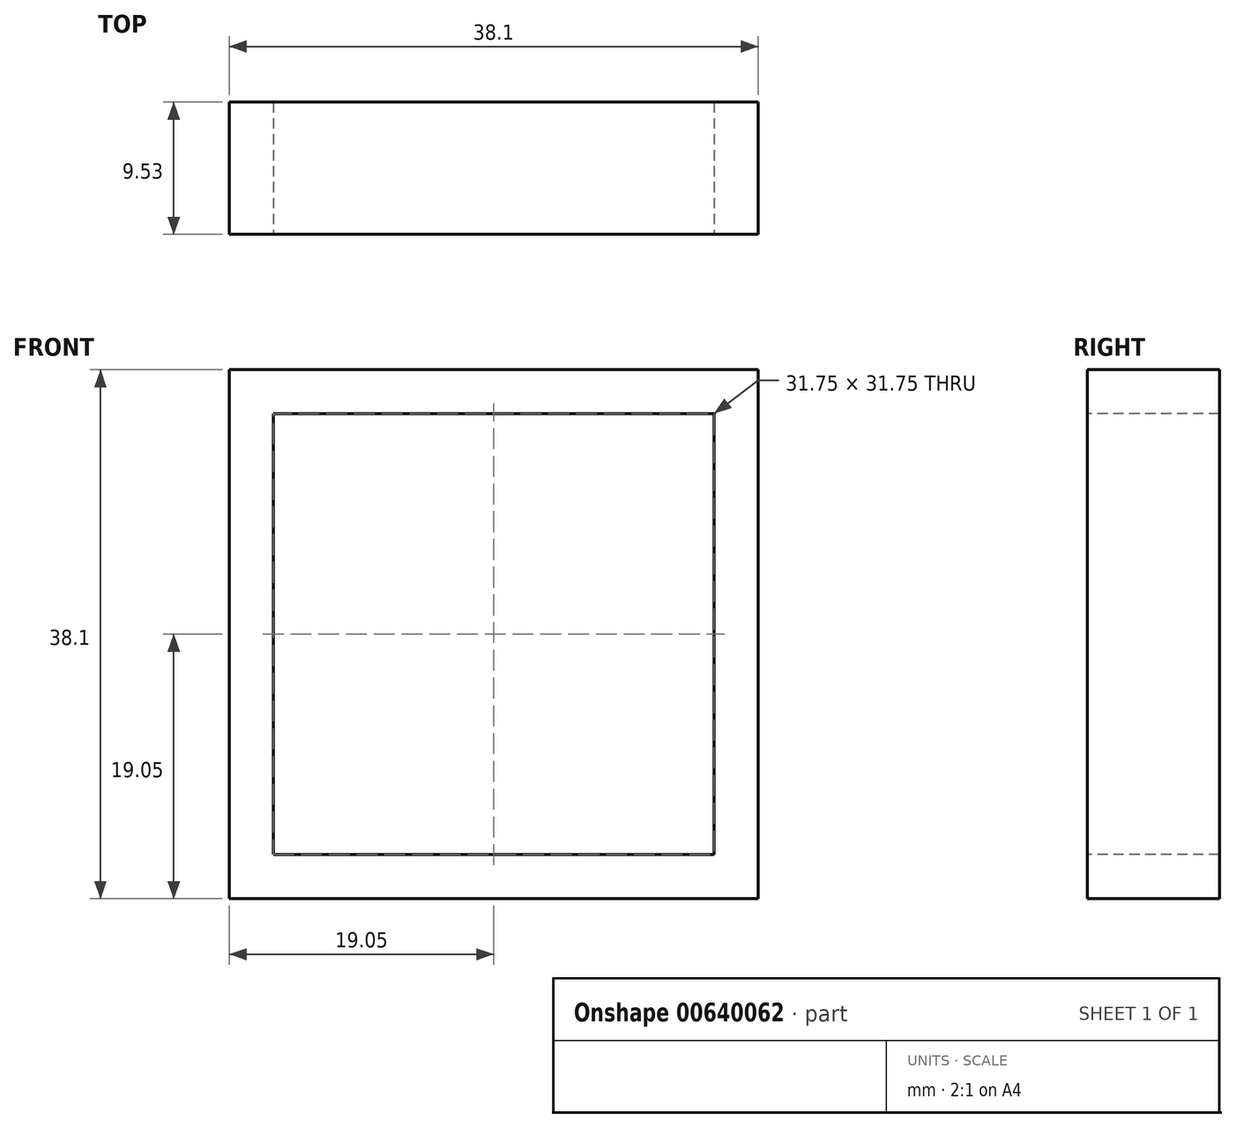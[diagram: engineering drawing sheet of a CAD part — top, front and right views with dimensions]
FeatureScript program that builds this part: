
annotation { "Feature Type Name" : "Feature", "Feature Type Description" : "" }
export const myFeature = defineFeature(function(context is Context, id is Id, definition is map)
    precondition{}
    {
        {
            var Q0;
            Q0=qCreatedBy(makeId("Front.planeOp"),FACE);
            var sketch = newSketch(context, id + "F0", { "sketchPlane" : qUnion([Q0])});
            skLineSegment(sketch, "E0", {"start": v(0, 0) * mm, "end": v(38.1, 0) * mm});
            skLineSegment(sketch, "E1", {"start": v(38.1, 0) * mm, "end": v(38.1, 38.1) * mm});
            skLineSegment(sketch, "E2", {"start": v(38.1, 38.1) * mm, "end": v(0, 38.1) * mm});
            skLineSegment(sketch, "E3", {"start": v(0, 38.1) * mm, "end": v(0, 0) * mm});
            skLineSegment(sketch, "E4", {"start": v(38.1, 0) * mm, "end": v(34.93, 0) * mm});
            skLineSegment(sketch, "E5.0", {"start": v(3.18, 34.92) * mm, "end": v(3.18, 3.18) * mm});
            skLineSegment(sketch, "E5.1", {"start": v(34.92, 34.92) * mm, "end": v(3.17, 34.92) * mm});
            skLineSegment(sketch, "E5.2", {"start": v(34.93, 3.18) * mm, "end": v(34.92, 34.92) * mm});
            skLineSegment(sketch, "E5.3", {"start": v(3.18, 3.18) * mm, "end": v(34.93, 3.18) * mm});
            skSolve(sketch);
        }
        {
            var Q0;
            Q0 = qSketchRegion(id + "F0", true);
            extrude(context, id + "F1", {"entities" : qUnion([Q0]), "oppositeDirection" : true, "depth" : 9.52 * mm, "offsetDistance" : 25.4 * mm});
        }
    });
